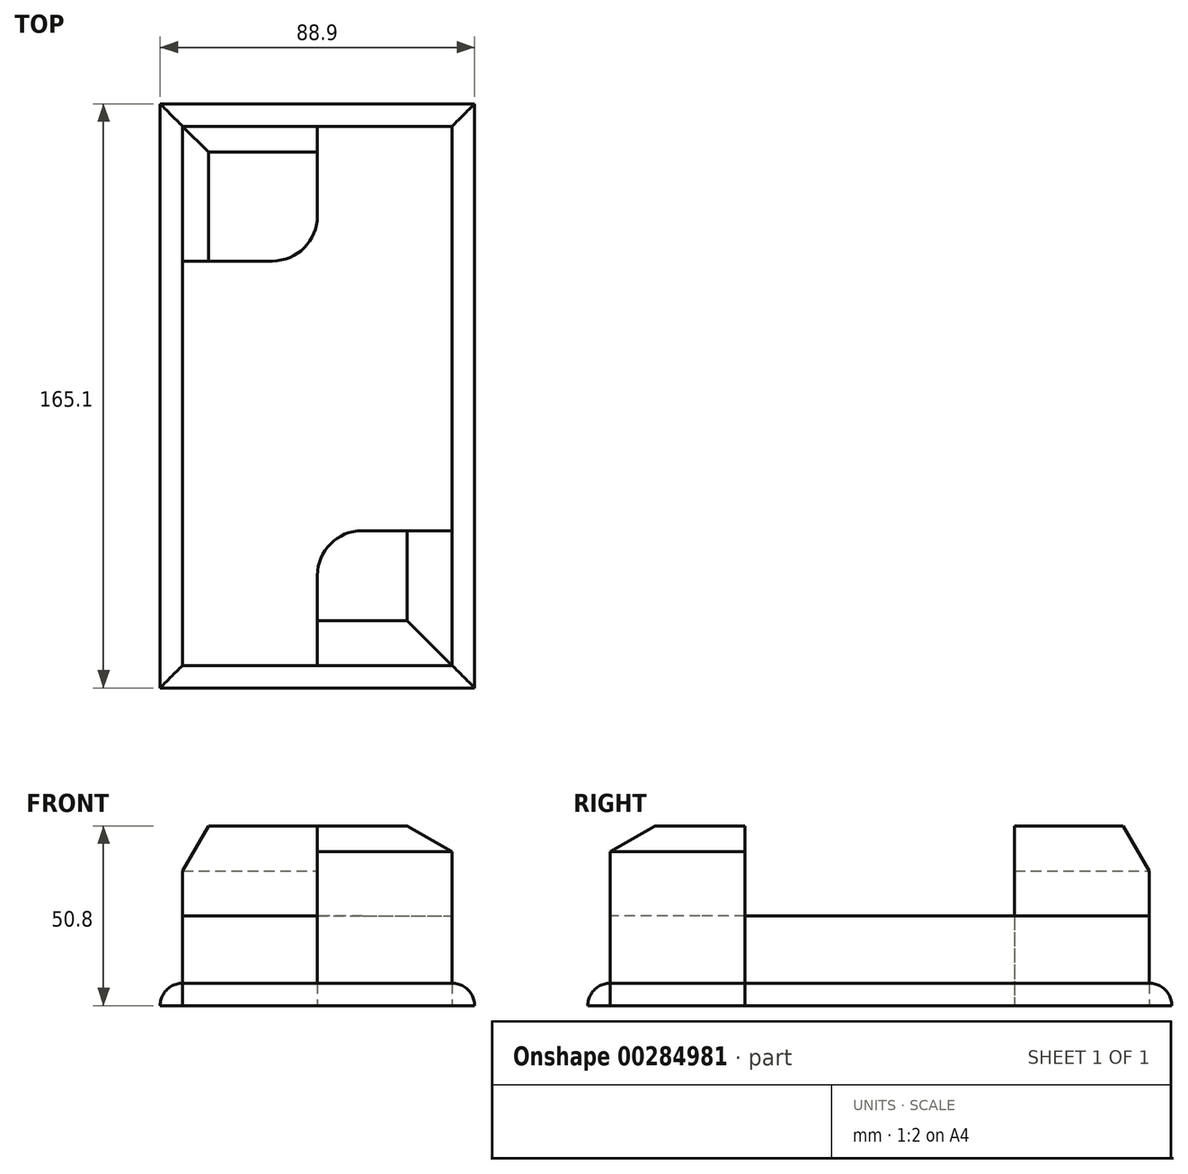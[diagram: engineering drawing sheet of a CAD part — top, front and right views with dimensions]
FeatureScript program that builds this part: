
annotation { "Feature Type Name" : "Feature", "Feature Type Description" : "" }
export const myFeature = defineFeature(function(context is Context, id is Id, definition is map)
    precondition{}
    {
        {
            var Q0;
            Q0=qCreatedBy(makeId("Top.planeOp"),FACE);
            var sketch = newSketch(context, id + "F0", { "sketchPlane" : qUnion([Q0])});
            skLineSegment(sketch, "E0.bottom", {"start": v(-41.62, 60.62) * mm, "end": v(47.28, 60.62) * mm});
            skLineSegment(sketch, "E0.top", {"start": v(-41.62, -104.48) * mm, "end": v(47.28, -104.48) * mm});
            skLineSegment(sketch, "E0.left", {"start": v(-41.62, 60.62) * mm, "end": v(-41.62, -104.48) * mm});
            skLineSegment(sketch, "E0.right", {"start": v(47.28, 60.62) * mm, "end": v(47.28, -104.48) * mm});
            skLineSegment(sketch, "E1.0", {"start": v(-35.27, 54.27) * mm, "end": v(40.93, 54.27) * mm});
            skLineSegment(sketch, "E1.1", {"start": v(-35.27, 54.27) * mm, "end": v(-35.27, -98.13) * mm});
            skLineSegment(sketch, "E1.2", {"start": v(-35.27, -98.13) * mm, "end": v(40.93, -98.13) * mm});
            skLineSegment(sketch, "E1.3", {"start": v(40.93, 54.27) * mm, "end": v(40.93, -98.13) * mm});
            skCircle(sketch, "E2", {"center": v(-9.87, 28.87) * mm, "radius": 12.7 * mm});
            skCircle(sketch, "E3", {"center": v(15.53, -72.73) * mm, "radius": 12.7 * mm});
            skLineSegment(sketch, "E4", {"start": v(2.83, 28.87) * mm, "end": v(2.83, 54.27) * mm});
            skLineSegment(sketch, "E5", {"start": v(-9.87, 16.17) * mm, "end": v(-35.27, 16.17) * mm});
            skLineSegment(sketch, "E6", {"start": v(2.83, -72.73) * mm, "end": v(2.83, -98.13) * mm});
            skLineSegment(sketch, "E7", {"start": v(15.53, -60.03) * mm, "end": v(40.93, -60.03) * mm});
            skSolve(sketch);
        }
        {
            var Q0;
            {var subQ0=sQuery(id+"F0.wireOp",EDGE,"E4");Q0=makeQuery(id+"F0.imprint","IMPRINT",FACE,{"disambiguationData":[TD([[makeQuery(id+"F0.imprint","IMPRINT",EDGE,{"derivedFrom":subQ0}),1.0]])]});}
            var Q1;
            {var subQ0=sQuery(id+"F0.wireOp",EDGE,"E2");var subQ1=makeQuery(id+"F0.imprint","INTERSECT",VERTEX,{"derivedFrom":[subQ0,sQuery(id+"F0.wireOp",EDGE,"E4")]});Q1=makeQuery(id+"F0.imprint","IMPRINT",FACE,{"disambiguationData":[TD([[makeQuery(id+"F0.imprint","IMPRINT",EDGE,{"disambiguationData":[TD([[subQ1,-1.0]])],"derivedFrom":subQ0}),1.0]])]});}
            var Q2;
            {var subQ0=sQuery(id+"F0.wireOp",EDGE,"E3");var subQ1=makeQuery(id+"F0.imprint","INTERSECT",VERTEX,{"derivedFrom":[subQ0,sQuery(id+"F0.wireOp",EDGE,"E6")]});Q2=makeQuery(id+"F0.imprint","IMPRINT",FACE,{"disambiguationData":[TD([[makeQuery(id+"F0.imprint","IMPRINT",EDGE,{"disambiguationData":[TD([[subQ1,1.0]])],"derivedFrom":subQ0}),1.0]])]});}
            var Q3;
            {var subQ0=sQuery(id+"F0.wireOp",EDGE,"E6");Q3=makeQuery(id+"F0.imprint","IMPRINT",FACE,{"disambiguationData":[TD([[makeQuery(id+"F0.imprint","IMPRINT",EDGE,{"derivedFrom":subQ0}),1.0]])]});}
            extrude(context, id + "F1", {"entities" : qUnion([Q0, Q1, Q2, Q3]), "depth" : 50.8 * mm});
        }
        {
            var Q0;
            {var subQ9=sQuery(id+"F0.wireOp",EDGE,"E4");Q0=makeQuery(id+"F0.imprint","IMPRINT",FACE,{"disambiguationData":[TD([[makeQuery(id+"F0.imprint","IMPRINT",EDGE,{"derivedFrom":subQ9}),-1.0]])]});}
            extrude(context, id + "F2", {"entities" : qUnion([Q0]), "depth" : 25.4 * mm});
        }
        {
            var Q0;
            Q0=makeQuery(id+"F0.imprint","IMPRINT",FACE,{"disambiguationData":[TD([[makeQuery(id+"F0.imprint","IMPRINT",EDGE,{"derivedFrom":sQuery(id+"F0.wireOp",EDGE,"E0.bottom")}),-1.0]])]});
            extrude(context, id + "F3", {"entities" : qUnion([Q0]), "depth" : 6.35 * mm});
        }
        {
            var Q0;
            Q0=makeQuery(id+"F1.opExtrude","CAP_EDGE",EDGE,{"disambiguationData":[OSD([sQuery(id+"F0.wireOp",EDGE,"E1.2")])],"isStart":false});
            var Q1;
            Q1=makeQuery(id+"F1.opExtrude","CAP_EDGE",EDGE,{"disambiguationData":[OSD([sQuery(id+"F0.wireOp",EDGE,"E1.3")])],"isStart":false});
            chamfer(context, id + "F4", {"entities" : qUnion([Q0, Q1]), "chamferType" : ChamferType.OFFSET_ANGLE, "width" : 12.7 * mm, "oppositeDirection" : false, "angle" : 30 * degree});
        }
        {
            var Q0;
            Q0=makeQuery(id+"F1.opExtrude","CAP_EDGE",EDGE,{"disambiguationData":[OSD([sQuery(id+"F0.wireOp",EDGE,"E1.0")])],"isStart":false});
            var Q1;
            Q1=makeQuery(id+"F1.opExtrude","CAP_EDGE",EDGE,{"disambiguationData":[OSD([sQuery(id+"F0.wireOp",EDGE,"E1.1")])],"isStart":false});
            chamfer(context, id + "F5", {"entities" : qUnion([Q0, Q1]), "chamferType" : ChamferType.OFFSET_ANGLE, "width" : 12.7 * mm, "oppositeDirection" : false, "angle" : 30 * degree});
        }
        {
            var Q0;
            Q0=makeQuery(id+"F3.opExtrude","CAP_EDGE",EDGE,{"disambiguationData":[OSD([sQuery(id+"F0.wireOp",EDGE,"E0.right")])],"isStart":false});
            var Q1;
            Q1=makeQuery(id+"F3.opExtrude","CAP_EDGE",EDGE,{"disambiguationData":[OSD([sQuery(id+"F0.wireOp",EDGE,"E0.bottom")])],"isStart":false});
            var Q2;
            Q2=makeQuery(id+"F3.opExtrude","CAP_EDGE",EDGE,{"disambiguationData":[OSD([sQuery(id+"F0.wireOp",EDGE,"E0.left")])],"isStart":false});
            var Q3;
            Q3=makeQuery(id+"F3.opExtrude","CAP_EDGE",EDGE,{"disambiguationData":[OSD([sQuery(id+"F0.wireOp",EDGE,"E0.top")])],"isStart":false});
            fillet(context, id + "F6", {"entities" : qUnion([Q0, Q1, Q2, Q3]), "radius" : 6.35 * mm, "tangentPropagation" : true, "allowEdgeOverflow" : false});
        }
    });
